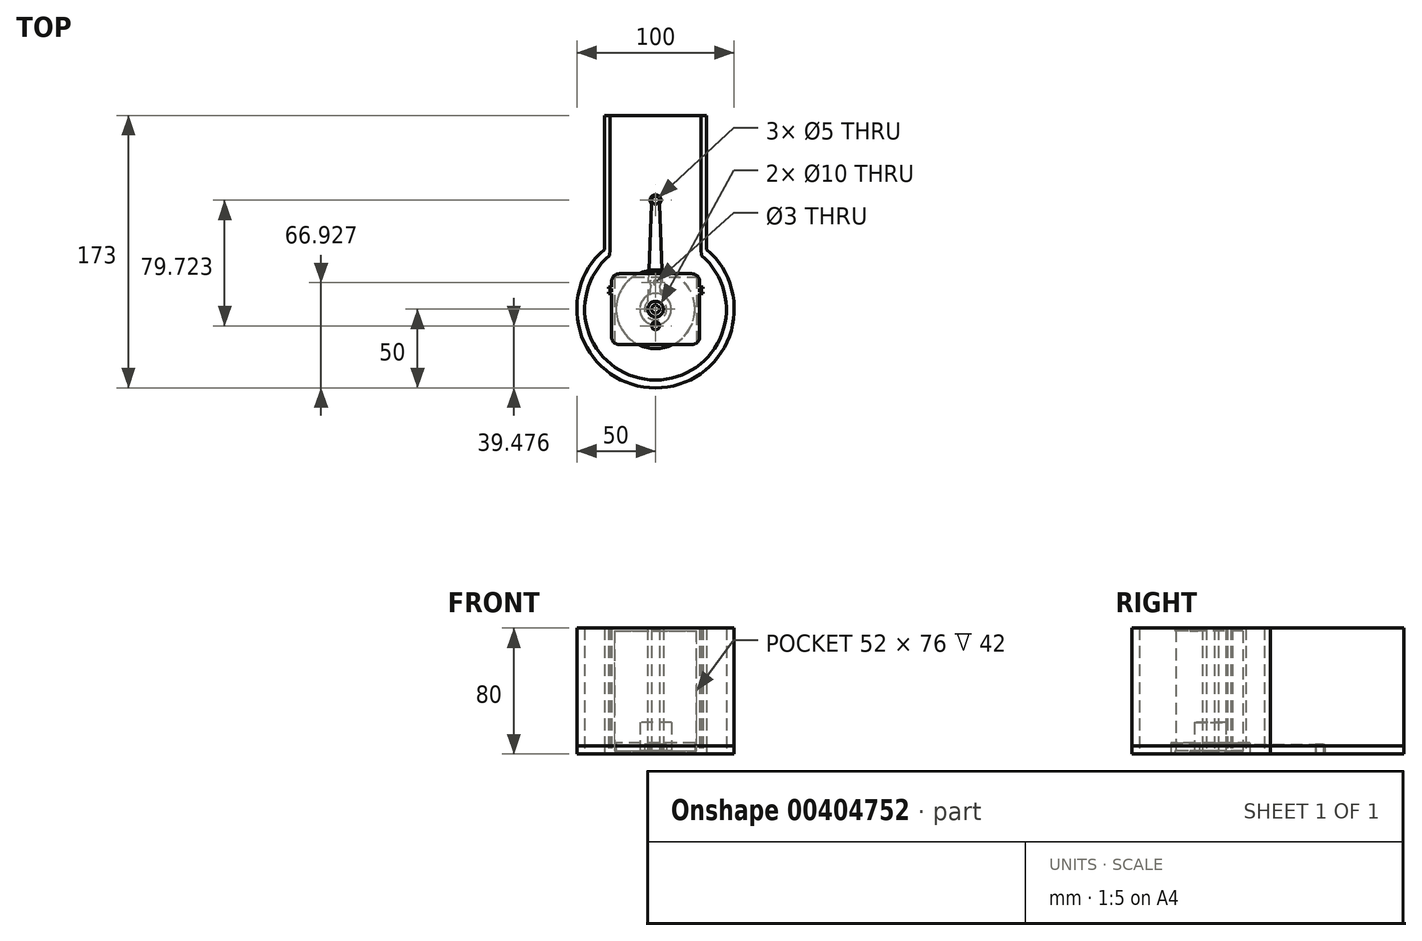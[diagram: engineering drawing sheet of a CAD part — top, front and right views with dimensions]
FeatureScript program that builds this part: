
annotation { "Feature Type Name" : "Feature", "Feature Type Description" : "" }
export const myFeature = defineFeature(function(context is Context, id is Id, definition is map)
    precondition{}
    {
        {
            var Q0;
            Q0=qCreatedBy(makeId("Top.planeOp"),FACE);
            var sketch = newSketch(context, id + "F0", { "sketchPlane" : qUnion([Q0])});
            skArc(sketch, "E0", {"start": v(-32.5, 38) * mm, "mid": v(0, -50) * mm, "end": v(32.5, 38) * mm});
            skLineSegment(sketch, "E1", {"start": v(-32.5, 38) * mm, "end": v(-32.5, 123) * mm});
            skLineSegment(sketch, "E2.MirrorCS", {"start": v(32.5, 38) * mm, "end": v(32.5, 123) * mm});
            skArc(sketch, "E3.0", {"start": v(-29.25, 34.2) * mm, "mid": v(0, -45) * mm, "end": v(29.25, 34.2) * mm});
            skLineSegment(sketch, "E4.0", {"start": v(-29, 38) * mm, "end": v(-29, 123) * mm});
            skLineSegment(sketch, "E5", {"start": v(-29, 38) * mm, "end": v(-29.25, 34.2) * mm});
            skLineSegment(sketch, "E6.MirrorCS", {"start": v(29, 38) * mm, "end": v(29.25, 34.2) * mm});
            skLineSegment(sketch, "E7.MirrorCS", {"start": v(29, 38) * mm, "end": v(29, 123) * mm});
            skLineSegment(sketch, "E8", {"start": v(-32.5, 123) * mm, "end": v(-29, 123) * mm});
            skLineSegment(sketch, "E9", {"start": v(29, 123) * mm, "end": v(32.5, 123) * mm});
            skSolve(sketch);
        }
        {
            var Q0;
            Q0 = qSketchRegion(id + "F0", true);
            extrude(context, id + "F1", {"entities" : qUnion([Q0]), "depth" : 80 * mm});
        }
        {
            var Q0;
            Q0=qCreatedBy(makeId("Top.planeOp"),FACE);
            var sketch = newSketch(context, id + "F2", { "sketchPlane" : qUnion([Q0])});
            skArc(sketch, "E10", {"start": v(-32.5, 38) * mm, "mid": v(0, -50) * mm, "end": v(32.5, 38) * mm});
            skLineSegment(sketch, "E11", {"start": v(-32.5, 38) * mm, "end": v(-32.5, 123) * mm});
            skLineSegment(sketch, "E12.MirrorCS", {"start": v(32.5, 38) * mm, "end": v(32.5, 123) * mm});
            skLineSegment(sketch, "E13", {"start": v(-32.5, 123) * mm, "end": v(32.5, 123) * mm});
            skSolve(sketch);
        }
        {
            var Q0;
            Q0 = qSketchRegion(id + "F2", true);
            extrude(context, id + "F3", {"entities" : qUnion([Q0]), "depth" : 5 * mm});
        }
        {
            var Q0;
            Q0=qCreatedBy(makeId("Top.planeOp"),FACE);
            var sketch = newSketch(context, id + "F4", { "sketchPlane" : qUnion([Q0])});
            skCircle(sketch, "E14", {"center": v(0, 0) * mm, "radius": 5 * mm});
            skSolve(sketch);
        }
        {
            var Q0;
            Q0 = qSketchRegion(id + "F4", true);
            extrude(context, id + "F5", {"entities" : qUnion([Q0]), "depth" : 80 * mm});
        }
        {
            var Q0;
            Q0=qCreatedBy(makeId("Top.planeOp"),FACE);
            var sketch = newSketch(context, id + "F6", { "sketchPlane" : qUnion([Q0])});
            skCircle(sketch, "E15", {"center": v(0, 0) * mm, "radius": 10 * mm});
            skCircle(sketch, "E16", {"center": v(0, 0) * mm, "radius": 5 * mm});
            skLineSegment(sketch, "E17", {"start": v(-3.61, 9.32) * mm, "end": v(-2.77, 14.78) * mm});
            skLineSegment(sketch, "E18.MirrorCS", {"start": v(3.61, 9.32) * mm, "end": v(2.77, 14.78) * mm});
            skCircle(sketch, "E19", {"center": v(0, 16.93) * mm, "radius": 3.5 * mm});
            skPoint(sketch, "E19.second.point", {"position": v(0, 20.43) * mm});
            skCircle(sketch, "E20.0", {"center": v(0, 16.93) * mm, "radius": 1.5 * mm});
            skPoint(sketch, "E21.trimOffspring.end.orphan", {"position": v(-1.99, 19.8) * mm});
            skPoint(sketch, "E22.orphan", {"position": v(1.99, 19.8) * mm});
            skSolve(sketch);
        }
        {
            var Q0;
            Q0=qCreatedBy(makeId("Top.planeOp"),FACE);
            var sketch = newSketch(context, id + "F7", { "sketchPlane" : qUnion([Q0])});
            skCircle(sketch, "E23", {"center": v(0, 0) * mm, "radius": 25 * mm});
            skSolve(sketch);
        }
        {
            var Q0;
            Q0=makeQuery(id+"F7.imprint","IMPRINT",FACE,{"disambiguationData":[TD([[makeQuery(id+"F7.imprint","IMPRINT",EDGE,{"derivedFrom":sQuery(id+"F7.wireOp",EDGE,"E23")}),1.0]])]});
            extrude(context, id + "F8", {"entities" : qUnion([Q0]), "depth" : 7 * mm});
        }
        {
            var Q0;
            Q0=qCreatedBy(makeId("Top.planeOp"),FACE);
            var sketch = newSketch(context, id + "F9", { "sketchPlane" : qUnion([Q0])});
            skCircle(sketch, "E24", {"center": v(0, 0) * mm, "radius": 5 * mm});
            skLineSegment(sketch, "E25", {"start": v(0, 66.7) * mm, "end": v(0, 69.2) * mm});
            skCircle(sketch, "E26", {"center": v(0, 69.2) * mm, "radius": 2.5 * mm});
            skLineSegment(sketch, "E27", {"start": v(-5, 0) * mm, "end": v(-4.99, 0.36) * mm});
            skPoint(sketch, "E28.orphan", {"position": v(0, 5) * mm});
            skLineSegment(sketch, "E29.MirrorCS", {"start": v(5, 0) * mm, "end": v(4.99, 0.36) * mm});
            skArc(sketch, "E30.0", {"start": v(2.59, 66.84) * mm, "mid": v(0, 72.7) * mm, "end": v(-2.59, 66.84) * mm});
            skPoint(sketch, "E31.orphan", {"position": v(2.5, 69.29) * mm});
            skPoint(sketch, "E32.orphan", {"position": v(-2.5, 69.29) * mm});
            skArc(sketch, "E33.0", {"start": v(-4.82, 5.08) * mm, "mid": v(0, -7) * mm, "end": v(4.82, 5.08) * mm});
            skLineSegment(sketch, "E34.trimOffspring", {"start": v(4.82, 5.08) * mm, "end": v(2.59, 66.84) * mm});
            skLineSegment(sketch, "E35.trimOffspring", {"start": v(-4.82, 5.08) * mm, "end": v(-2.59, 66.84) * mm});
            skSolve(sketch);
        }
        {
            var Q0;
            Q0 = qSketchRegion(id + "F9", true);
            extrude(context, id + "F10", {"entities" : qUnion([Q0]), "depth" : 6 * mm});
        }
        {
            var Q0;
            Q0 = qSketchRegion(id + "F6", true);
            extrude(context, id + "F11", {"entities" : qUnion([Q0]), "depth" : 2 * mm});
        }
        {
            var Q0;
            Q0=qCreatedBy(makeId("Top.planeOp"),FACE);
            var sketch = newSketch(context, id + "F12", { "sketchPlane" : qUnion([Q0])});
            skLineSegment(sketch, "E36.bottom", {"start": v(-28, 22.5) * mm, "end": v(28, 22.5) * mm});
            skLineSegment(sketch, "E36.top", {"start": v(-28, -22.5) * mm, "end": v(28, -22.5) * mm});
            skLineSegment(sketch, "E36.left", {"start": v(-28, 22.5) * mm, "end": v(-28, -22.5) * mm});
            skLineSegment(sketch, "E36.right", {"start": v(28, 22.5) * mm, "end": v(28, -22.5) * mm});
            skPoint(sketch, "E36.middle", {"position": v(0, 0) * mm});
            skLineSegment(sketch, "E37", {"start": v(-28, 14.1) * mm, "end": v(-30, 14.1) * mm});
            skLineSegment(sketch, "E38", {"start": v(-30, 14.1) * mm, "end": v(-30, 13.1) * mm});
            skLineSegment(sketch, "E39", {"start": v(-30, 13.1) * mm, "end": v(-28, 13.1) * mm});
            skLineSegment(sketch, "E40.MirrorCS", {"start": v(-28, 9.9) * mm, "end": v(-30, 9.9) * mm});
            skLineSegment(sketch, "E41.MirrorCS", {"start": v(-30, 9.9) * mm, "end": v(-30, 10.9) * mm});
            skLineSegment(sketch, "E42.MirrorCS", {"start": v(-30, 10.9) * mm, "end": v(-28, 10.9) * mm});
            skLineSegment(sketch, "E43.MirrorCS", {"start": v(28, 14.1) * mm, "end": v(30, 14.1) * mm});
            skLineSegment(sketch, "E44.MirrorCS", {"start": v(30, 14.1) * mm, "end": v(30, 13.1) * mm});
            skLineSegment(sketch, "E45.MirrorCS", {"start": v(30, 13.1) * mm, "end": v(28, 13.1) * mm});
            skLineSegment(sketch, "E46.MirrorCS", {"start": v(30, 10.9) * mm, "end": v(28, 10.9) * mm});
            skLineSegment(sketch, "E47.MirrorCS", {"start": v(30, 9.9) * mm, "end": v(30, 10.9) * mm});
            skLineSegment(sketch, "E48.MirrorCS", {"start": v(28, 9.9) * mm, "end": v(30, 9.9) * mm});
            skCircle(sketch, "E49", {"center": v(0, -10.52) * mm, "radius": 2.5 * mm});
            skSolve(sketch);
        }
        {
            var Q0;
            {var subQ4=sQuery(id+"F12.wireOp",EDGE,"E36.bottom");Q0=makeQuery(id+"F12.imprint","IMPRINT",FACE,{"disambiguationData":[TD([[makeQuery(id+"F12.imprint","IMPRINT",EDGE,{"derivedFrom":subQ4}),-1.0]])]});}
            var Q1;
            {var subQ0=sQuery(id+"F12.wireOp",EDGE,"E37");Q1=makeQuery(id+"F12.imprint","IMPRINT",FACE,{"disambiguationData":[TD([[makeQuery(id+"F12.imprint","IMPRINT",EDGE,{"derivedFrom":subQ0}),1.0]])]});}
            var Q2;
            {var subQ0=sQuery(id+"F12.wireOp",EDGE,"E40.MirrorCS");Q2=makeQuery(id+"F12.imprint","IMPRINT",FACE,{"disambiguationData":[TD([[makeQuery(id+"F12.imprint","IMPRINT",EDGE,{"derivedFrom":subQ0}),-1.0]])]});}
            var Q3;
            {var subQ0=sQuery(id+"F12.wireOp",EDGE,"E43.MirrorCS");Q3=makeQuery(id+"F12.imprint","IMPRINT",FACE,{"disambiguationData":[TD([[makeQuery(id+"F12.imprint","IMPRINT",EDGE,{"derivedFrom":subQ0}),-1.0]])]});}
            var Q4;
            {var subQ0=sQuery(id+"F12.wireOp",EDGE,"E46.MirrorCS");Q4=makeQuery(id+"F12.imprint","IMPRINT",FACE,{"disambiguationData":[TD([[makeQuery(id+"F12.imprint","IMPRINT",EDGE,{"derivedFrom":subQ0}),1.0]])]});}
            extrude(context, id + "F13", {"entities" : qUnion([Q0, Q1, Q2, Q3, Q4]), "depth" : 80 * mm});
        }
        {
            var Q0;
            Q0=makeQuery(id+"F13.opExtrude","SWEPT_FACE",FACE,{"disambiguationData":[OSD([sQuery(id+"F12.wireOp",EDGE,"E36.top")])]});
            var Q1;
            Q1=makeQuery(id+"F13.opExtrude","SWEPT_FACE",FACE,{"disambiguationData":[OSD([sQuery(id+"F12.wireOp",EDGE,"E49")])]});
            shell(context, id + "F14", {"entities" : qUnion([Q0, Q1]), "thickness" : 2 * mm});
        }
        {
            var Q0;
            Q0=makeQuery(id+"F13.opExtrude","SWEPT_EDGE",EDGE,{"disambiguationData":[OSD([sQuery(id+"F12.wireOp",EDGE,"E36.bottom"),sQuery(id+"F12.wireOp",EDGE,"E36.left")])]});
            var Q1;
            Q1=makeQuery(id+"F13.opExtrude","SWEPT_EDGE",EDGE,{"disambiguationData":[OSD([sQuery(id+"F12.wireOp",EDGE,"E36.bottom"),sQuery(id+"F12.wireOp",EDGE,"E36.right")])]});
            var Q2;
            Q2=makeQuery(id+"F13.opExtrude","SWEPT_EDGE",EDGE,{"disambiguationData":[OSD([sQuery(id+"F12.wireOp",EDGE,"E36.top"),sQuery(id+"F12.wireOp",EDGE,"E36.right")])]});
            var Q3;
            Q3=makeQuery(id+"F13.opExtrude","SWEPT_EDGE",EDGE,{"disambiguationData":[OSD([sQuery(id+"F12.wireOp",EDGE,"E36.top"),sQuery(id+"F12.wireOp",EDGE,"E36.left")])]});
            fillet(context, id + "F15", {"entities" : qUnion([Q0, Q1, Q2, Q3]), "radius" : 5 * mm, "tangentPropagation" : true, "allowEdgeOverflow" : false});
        }
        {
            var Q0;
            Q0=qCreatedBy(makeId("Top.planeOp"),FACE);
            var sketch = newSketch(context, id + "F16", { "sketchPlane" : qUnion([Q0])});
            skCircle(sketch, "E50", {"center": v(0, 0) * mm, "radius": 2.5 * mm});
            skSolve(sketch);
        }
        {
            var Q0;
            Q0 = qSketchRegion(id + "F16", true);
            extrude(context, id + "F17", {"entities" : qUnion([Q0]), "depth" : 80 * mm});
        }
        {
            var Q0;
            Q0=qCreatedBy(makeId("Top.planeOp"),FACE);
            var sketch = newSketch(context, id + "F18", { "sketchPlane" : qUnion([Q0])});
            skCircle(sketch, "E51", {"center": v(0, 0) * mm, "radius": 10 * mm});
            skSolve(sketch);
        }
        {
            var Q0;
            Q0 = qSketchRegion(id + "F18", true);
            extrude(context, id + "F19", {"entities" : qUnion([Q0]), "depth" : 20 * mm});
        }
    });
